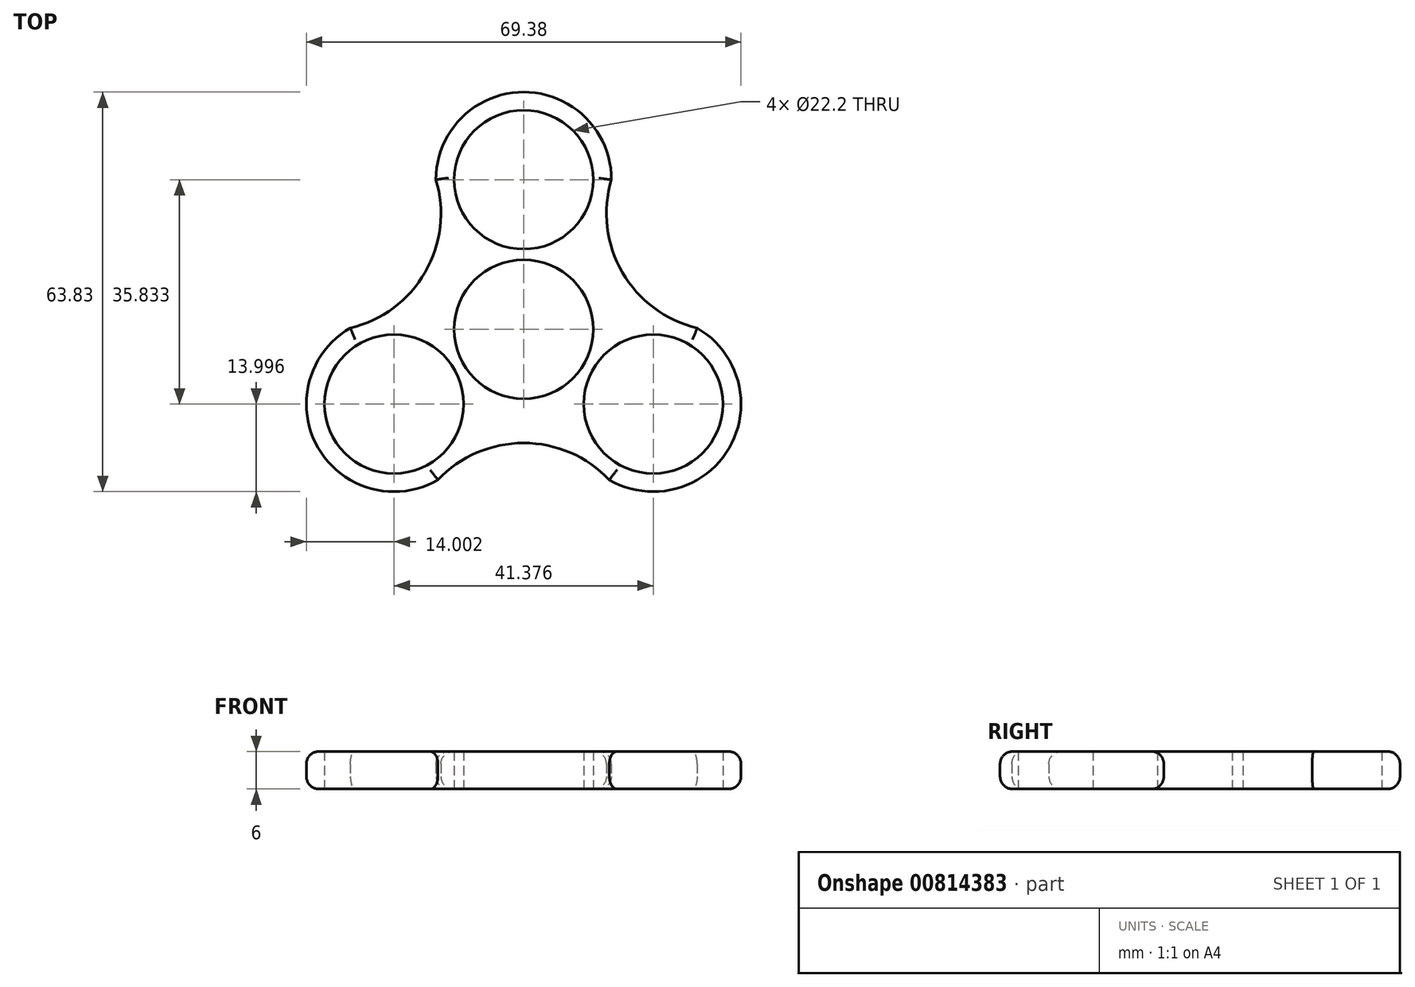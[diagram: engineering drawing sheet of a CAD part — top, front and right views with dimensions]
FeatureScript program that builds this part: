
annotation { "Feature Type Name" : "Feature", "Feature Type Description" : "" }
export const myFeature = defineFeature(function(context is Context, id is Id, definition is map)
    precondition{}
    {
        {
            var Q0;
            Q0=qCreatedBy(makeId("Top.planeOp"),FACE);
            var sketch = newSketch(context, id + "F0", { "sketchPlane" : qUnion([Q0])});
            skCircle(sketch, "E0", {"center": v(0, 0) * mm, "radius": 11.1 * mm});
            skCircle(sketch, "E1", {"center": v(0, 0) * mm, "radius": 3.75 * mm});
            skCircle(sketch, "E2", {"center": v(0, 23.89) * mm, "radius": 11.1 * mm});
            skCircle(sketch, "E3", {"center": v(0, 23.89) * mm, "radius": 3.75 * mm});
            skCircle(sketch, "E4.1.0", {"center": v(-20.69, -11.94) * mm, "radius": 3.75 * mm});
            skCircle(sketch, "E4.1.1", {"center": v(-20.69, -11.94) * mm, "radius": 11.1 * mm});
            skCircle(sketch, "E4.2.0", {"center": v(20.69, -11.94) * mm, "radius": 3.75 * mm});
            skCircle(sketch, "E4.2.1", {"center": v(20.69, -11.94) * mm, "radius": 11.1 * mm});
            skLineSegment(sketch, "E5", {"start": v(-21.01, 24.56) * mm, "end": v(-21.01, 24.56) * mm});
            skArc(sketch, "E6", {"start": v(14, 23.86) * mm, "mid": v(0.01, 37.89) * mm, "end": v(-14, 23.89) * mm});
            skArc(sketch, "E7.1.0", {"start": v(-27.66, 0.2) * mm, "mid": v(-32.82, -18.93) * mm, "end": v(-13.69, -24.07) * mm});
            skArc(sketch, "E7.2.0", {"start": v(13.66, -24.05) * mm, "mid": v(32.8, -18.96) * mm, "end": v(27.69, 0.18) * mm});
            skArc(sketch, "E8", {"start": v(-27.66, 0.2) * mm, "mid": v(-15.73, 9.1) * mm, "end": v(-14, 23.89) * mm});
            skArc(sketch, "E9.1.0", {"start": v(13.66, -24.05) * mm, "mid": v(-0.02, -18.17) * mm, "end": v(-13.69, -24.07) * mm});
            skArc(sketch, "E9.2.0", {"start": v(14, 23.86) * mm, "mid": v(15.75, 9.07) * mm, "end": v(27.69, 0.18) * mm});
            skSolve(sketch);
        }
        {
            var Q0;
            Q0=makeQuery(id+"F0.imprint","IMPRINT",FACE,{"disambiguationData":[TD([[makeQuery(id+"F0.imprint","IMPRINT",EDGE,{"derivedFrom":sQuery(id+"F0.wireOp",EDGE,"E0")}),-1.0]])]});
            extrude(context, id + "F1", {"entities" : qUnion([Q0]), "depth" : 6 * mm, "offsetDistance" : 25 * mm});
        }
        {
            var Q0;
            Q0=makeQuery(id+"F1.opExtrude","CAP_EDGE",EDGE,{"disambiguationData":[OSD([sQuery(id+"F0.wireOp",EDGE,"E9.2.0")])],"isStart":true});
            var Q1;
            Q1=makeQuery(id+"F1.opExtrude","CAP_EDGE",EDGE,{"disambiguationData":[OSD([sQuery(id+"F0.wireOp",EDGE,"E6")])],"isStart":true});
            var Q2;
            Q2=makeQuery(id+"F1.opExtrude","CAP_EDGE",EDGE,{"disambiguationData":[OSD([sQuery(id+"F0.wireOp",EDGE,"E8")])],"isStart":true});
            var Q3;
            Q3=makeQuery(id+"F1.opExtrude","CAP_EDGE",EDGE,{"disambiguationData":[OSD([sQuery(id+"F0.wireOp",EDGE,"E7.1.0")])],"isStart":true});
            var Q4;
            Q4=makeQuery(id+"F1.opExtrude","CAP_EDGE",EDGE,{"disambiguationData":[OSD([sQuery(id+"F0.wireOp",EDGE,"E9.1.0")])],"isStart":true});
            var Q5;
            Q5=makeQuery(id+"F1.opExtrude","CAP_EDGE",EDGE,{"disambiguationData":[OSD([sQuery(id+"F0.wireOp",EDGE,"E7.2.0")])],"isStart":true});
            fillet(context, id + "F2", {"entities" : qUnion([Q0, Q1, Q2, Q3, Q4, Q5]), "radius" : 2 * mm, "tangentPropagation" : true, "allowEdgeOverflow" : false});
        }
        {
            var Q0;
            Q0=makeQuery(id+"F1.opExtrude","CAP_EDGE",EDGE,{"disambiguationData":[OSD([sQuery(id+"F0.wireOp",EDGE,"E7.2.0")])],"isStart":false});
            var Q1;
            Q1=makeQuery(id+"F1.opExtrude","CAP_EDGE",EDGE,{"disambiguationData":[OSD([sQuery(id+"F0.wireOp",EDGE,"E9.2.0")])],"isStart":false});
            var Q2;
            Q2=makeQuery(id+"F1.opExtrude","CAP_EDGE",EDGE,{"disambiguationData":[OSD([sQuery(id+"F0.wireOp",EDGE,"E6")])],"isStart":false});
            var Q3;
            Q3=makeQuery(id+"F1.opExtrude","CAP_EDGE",EDGE,{"disambiguationData":[OSD([sQuery(id+"F0.wireOp",EDGE,"E8")])],"isStart":false});
            var Q4;
            Q4=makeQuery(id+"F1.opExtrude","CAP_EDGE",EDGE,{"disambiguationData":[OSD([sQuery(id+"F0.wireOp",EDGE,"E7.1.0")])],"isStart":false});
            var Q5;
            Q5=makeQuery(id+"F1.opExtrude","CAP_EDGE",EDGE,{"disambiguationData":[OSD([sQuery(id+"F0.wireOp",EDGE,"E9.1.0")])],"isStart":false});
            fillet(context, id + "F3", {"entities" : qUnion([Q0, Q1, Q2, Q3, Q4, Q5]), "radius" : 2 * mm, "tangentPropagation" : true, "allowEdgeOverflow" : false});
        }
    });
